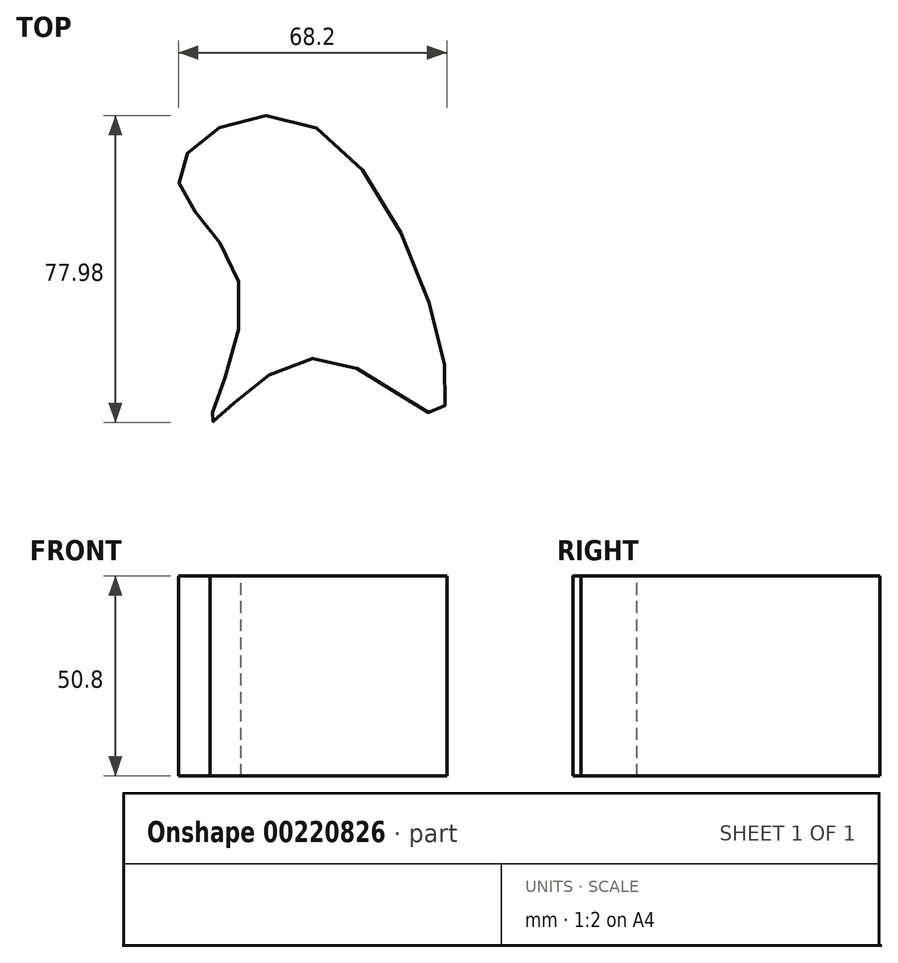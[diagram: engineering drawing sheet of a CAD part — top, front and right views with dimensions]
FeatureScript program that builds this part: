
annotation { "Feature Type Name" : "Feature", "Feature Type Description" : "" }
export const myFeature = defineFeature(function(context is Context, id is Id, definition is map)
    precondition{}
    {
        {
            var Q0;
            Q0=qCreatedBy(makeId("Top.planeOp"),FACE);
            var sketch = newSketch(context, id + "F0", { "sketchPlane" : qUnion([Q0])});
            skFitSpline(sketch, "E0", {"points": [v(0, 40.57) * mm, v(-35.01, 29.09) * mm, v(-19.45, 0) * mm, v(-26.86, -34.27) * mm, v(0, -17.97) * mm, v(31.68, -31.68) * mm, v(0, 40.57) * mm]});
            skSolve(sketch);
        }
        {
            var Q0;
            Q0=sQuery(id+"F0.wireOp",EDGE,"E0");
            extrude(context, id + "F1", {"bodyType" : ToolBodyType.SURFACE, "surfaceEntities" : qUnion([Q0]), "depth" : 50.8 * mm});
        }
    });
